# Revit family: Furniture-Floor_Mount-Vanity-KOHLER-HARKEN -K-33559
name_source: partatom
category: Casework
revit_build: Autodesk Revit 2017 (Build: 20160225_1515(x64)
units: mm (PartAtom-declared; Revit-internal decimal feet)

## family parameters
Cut with Voids When Loaded = No
Host = Face
OmniClass Number = 23.21.19.00
OmniClass Title = Casework
Room Calculation Point = No
Shared = No

## types (2) — shared parameters
ADA Compliant = No
Assembly Code = E2010.30
Construction Type = Floor Mount
Date Modified = 02/17/2021
Default Elevation = 0"
Depth = 21 7/8"
Description = VANITY 36 INCHES
Hardware Included = No
Height = 34 1/2"
Manufacturer = KOHLER Co.
Master Format 2014 = 12 35 30.23
Master Format 2014 Name = Bathroom Casework
Material = Solid Wood
Product Documentation Link = https://www.us.kohler.com
Product Name = HARKEN
Product Page URL = http://www.us.kohler.com
URL = https://www.us.kohler.com
WaterSense Certified = No
Width = 36"

## per-type parameters (varying)
| type | Finish | Model | Product Finish | Type |
| 1WA-Linen White | Kohler-Wood-1WA-Linen White | K-33559-1WA | Kohler-Wood-1WA-Linen_White | 1 |
| 1WX-New Dark Grey | Kohler-Wood-1WX-New_Dark_Grey | K-33559-1WX | KOHLER-Wood-1WX-New_Dark_Grey | 2 |

## geometry (parser evidence)
native form markers: Sweep x7
no freeform markers — native parametric forms only
